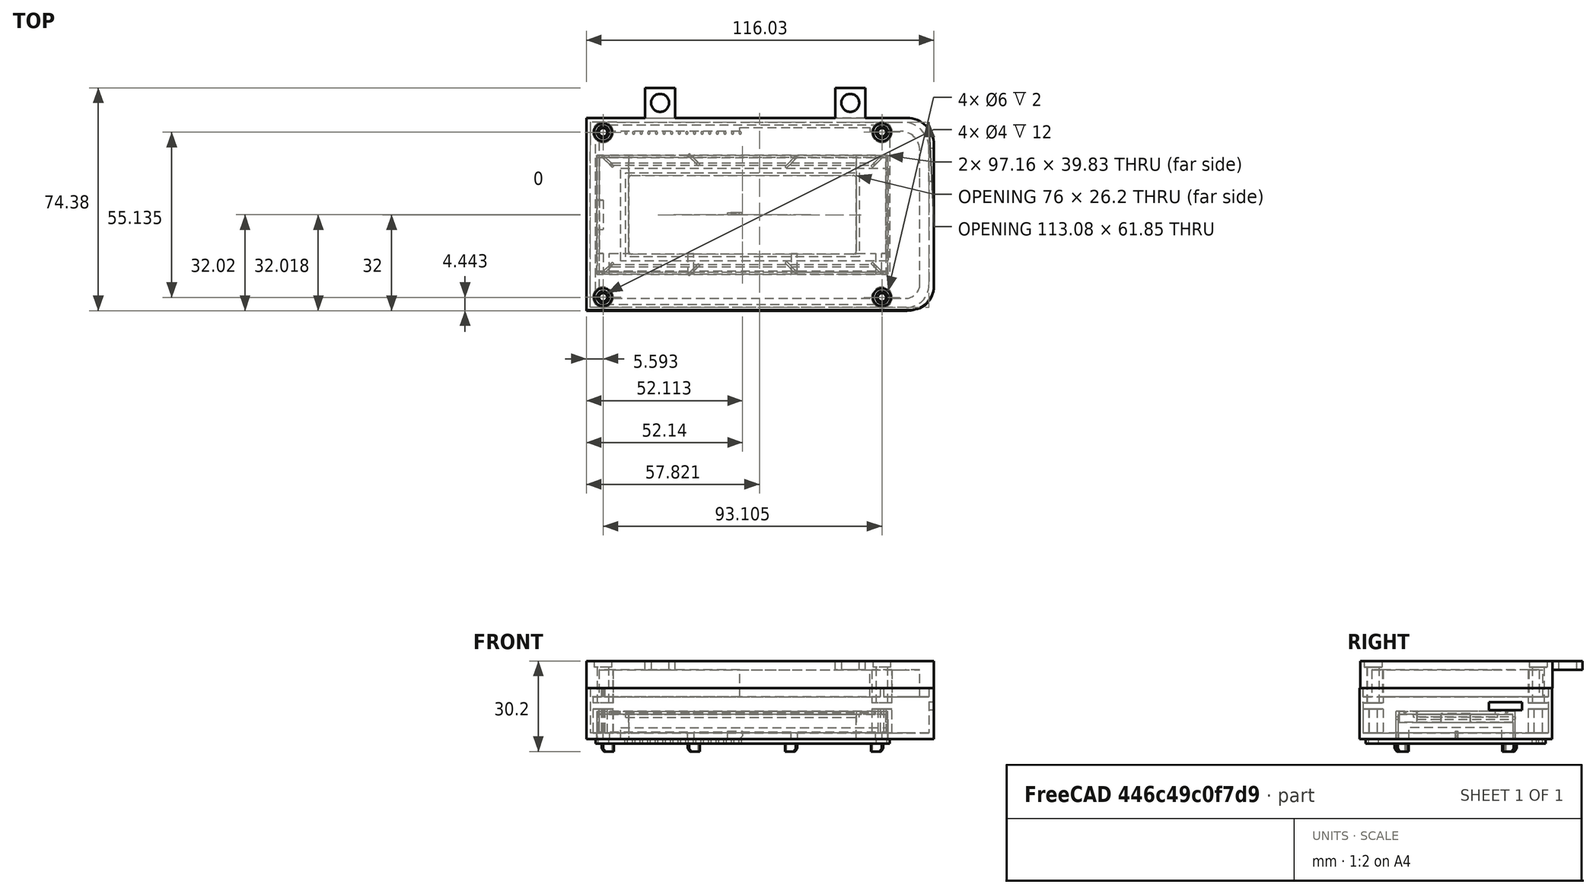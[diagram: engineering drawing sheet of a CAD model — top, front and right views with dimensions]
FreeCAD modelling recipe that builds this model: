
FCSTD DOCUMENT  (FreeCAD 0.18R13666 (Git))
Label: meteostation-lcd
License: CC-BY 3.0
LicenseURL: http://creativecommons.org/licenses/by/3.0/
objects: Sketcher::SketchObject×26, PartDesign::Body×14, PartDesign::Pocket×11, Part::Feature×10, App::DocumentObjectGroup×8, PartDesign::Pad×7, Part::Extrusion×5, Part::MultiFuse×4, PartDesign::FeatureBase×3, PartDesign::LinearPattern×1, Part::Mirroring×1, Part::Compound×1, PartDesign::Plane×1, PartDesign::ShapeBinder×1, App::Part×1, Mesh::Feature×1, PartDesign::Fillet×1, PartDesign::Hole×1
note: 106 computed .brp shape members not serialized (recipe doc carries the construction recipe); baked Part::Feature solids carry a one-line shape summary decoded from their .brp

FEATURE [Sketcher::SketchObject] Sketch001  label="backlight-sketch"
  MapMode = 5
  Support = -> [XY_Plane003]
  sketch-geometry (4):
    g0: LineSegment StartX=-40.6 StartY=15.5 StartZ=0 EndX=48.6 EndY=15.5 EndZ=0
    g1: LineSegment StartX=48.6 StartY=15.5 StartZ=0 EndX=48.6 EndY=-15.5 EndZ=0
    g2: LineSegment StartX=48.6 StartY=-15.5 StartZ=0 EndX=-40.6 EndY=-15.5 EndZ=0
    g3: LineSegment StartX=-40.6 StartY=-15.5 StartZ=0 EndX=-40.6 EndY=15.5 EndZ=0
  constraints (12):
    c: Coincident(g0,g1)
    c: Coincident(g1,g2)
    c: Coincident(g2,g3)
    c: Coincident(g3,g0)
    c: Horizontal(g0)
    c: Horizontal(g2)
    c: Vertical(g1)
    c: Vertical(g3)
    c: DistanceX(g-1,g1) = 48.6
    c: Symmetric(g0,g2,g-1)
    c: DistanceY(g-1,g0) = 15.5
    c: DistanceX(g-1,g0) = -40.6
FEATURE [PartDesign::Pad] Pad001  label="backlight"
  Length = 3.7
  Length2 = 100
  Profile = -> Sketch001
  Type = 0
FEATURE [Sketcher::SketchObject] Sketch002  label="metal-cover-main-sketch"
  MapMode = 5
  Support = -> [XY_Plane004]
  sketch-geometry (4):
    g0: LineSegment StartX=-48.5 StartY=19.85 StartZ=0 EndX=48.5 EndY=19.85 EndZ=0
    g1: LineSegment StartX=48.5 StartY=19.85 StartZ=0 EndX=48.5 EndY=-19.85 EndZ=0
    g2: LineSegment StartX=48.5 StartY=-19.85 StartZ=0 EndX=-48.5 EndY=-19.85 EndZ=0
    g3: LineSegment StartX=-48.5 StartY=-19.85 StartZ=0 EndX=-48.5 EndY=19.85 EndZ=0
  constraints (11):
    c: Coincident(g0,g1)
    c: Coincident(g1,g2)
    c: Coincident(g2,g3)
    c: Coincident(g3,g0)
    c: Horizontal(g0)
    c: Horizontal(g2)
    c: Vertical(g1)
    c: Vertical(g3)
    c: Symmetric(g0,g1,g-1)
    c: DistanceX(g0) = 97
    c: DistanceY(g1) = -39.7
FEATURE [PartDesign::Pad] Pad002  label="metal-cover"
  Length = 9.2
  Length2 = 100
  Profile = -> Sketch002
  Type = 0
FEATURE [Sketcher::SketchObject] Sketch003  label="bottom-cutout-1-sketch"
  ExternalGeometry = -> [Pad002]
  MapMode = 5
  Placement = pos=(0,0,0) rot=(1,0,0;3.14159rad)
  Support = -> [Pad002]
  sketch-geometry (5):
    g0: LineSegment StartX=-47.8 StartY=19.15 StartZ=0 EndX=47.8 EndY=19.15 EndZ=0
    g1: LineSegment StartX=47.8 StartY=19.15 StartZ=0 EndX=47.8 EndY=-19.15 EndZ=0
    g2: LineSegment StartX=47.8 StartY=-19.15 StartZ=0 EndX=-47.8 EndY=-19.15 EndZ=0
    g3: LineSegment StartX=-47.8 StartY=-19.15 StartZ=0 EndX=-47.8 EndY=19.15 EndZ=0
    g4: LineSegment [constr] StartX=-48.5 StartY=19.85 StartZ=0 EndX=-47.8 EndY=19.15 EndZ=0
  constraints (13):
    c: Coincident(g0,g1)
    c: Coincident(g1,g2)
    c: Coincident(g2,g3)
    c: Coincident(g3,g0)
    c: Horizontal(g0)
    c: Horizontal(g2)
    c: Vertical(g1)
    c: Vertical(g3)
    c: Symmetric(g0,g1,g-1)
    c: Coincident(g4,g-3)
    c: Coincident(g4,g0)
    c: Angle(g4,g-3) = 0.785398
    c: DistanceX(g0,g4) = -0.7
FEATURE [PartDesign::Pocket] Pocket  label="bottom-cutout-1"
  BaseFeature = -> Pad002
  Length = 8.2
  Length2 = 100
  Profile = -> Sketch003
  Type = 0
FEATURE [Sketcher::SketchObject] Sketch004  label="side-cutout-2-sketch"
  ExternalGeometry = -> [Pocket]
  MapMode = 5
  Placement = pos=(48.5,0,0) rot=(0.57735,0.57735,0.57735;2.0944rad)
  Support = -> [Pocket]
  sketch-geometry (7):
    g0: LineSegment StartX=19.15 StartY=5.5 StartZ=0 EndX=-19.15 EndY=5.5 EndZ=0
    g1: LineSegment StartX=-19.15 StartY=5.5 StartZ=0 EndX=-19.15 EndY=0 EndZ=0
    g2: LineSegment [constr] StartX=-19.15 StartY=0 StartZ=0 EndX=19.15 EndY=0 EndZ=0
    g3: LineSegment StartX=19.15 StartY=0 StartZ=0 EndX=19.15 EndY=5.5 EndZ=0
    g4: LineSegment StartX=-19.15 StartY=0 StartZ=0 EndX=-19.15 EndY=-1 EndZ=0
    g5: LineSegment StartX=-19.15 StartY=-1 StartZ=0 EndX=19.15 EndY=-1 EndZ=0
    g6: LineSegment StartX=19.15 StartY=-1 StartZ=0 EndX=19.15 EndY=0 EndZ=0
  constraints (19):
    c: Coincident(g0,g1)
    c: Coincident(g1,g2)
    c: Coincident(g2,g3)
    c: Coincident(g3,g0)
    c: Horizontal(g0)
    c: Horizontal(g2)
    c: Vertical(g1)
    c: Vertical(g3)
    c: Symmetric(g0,g0,g-2)
    c: DistanceY(g-3,g0) = -3.7
    c: Coincident(g2,g-4)
    c: Coincident(g4,g5)
    c: Coincident(g5,g6)
    c: Horizontal(g5)
    c: Vertical(g4)
    c: Vertical(g6)
    c: Coincident(g6,g2)
    c: Coincident(g4,g1)
    c: DistanceY(g4) = -1
FEATURE [PartDesign::Pocket] Pocket001  label="side-cutout-2"
  BaseFeature = -> Pocket
  Length = 5
  Length2 = 100
  Profile = -> Sketch004
  Type = 1
FEATURE [Sketcher::SketchObject] Sketch005  label="front-cutout-3-sketch"
  ExternalGeometry = -> [Pocket001]
  MapMode = 5
  Placement = pos=(0,0,5.5) rot=(1,0,0;3.14159rad)
  Support = -> [Pocket001]
  sketch-geometry (21):
    g0: LineSegment [constr] StartX=-48.5 StartY=12.85 StartZ=0 EndX=48.5 EndY=12.85 EndZ=0
    g1: LineSegment StartX=-16.25 StartY=12.85 StartZ=0 EndX=16.25 EndY=12.85 EndZ=0
    g2: LineSegment StartX=16.25 StartY=12.85 StartZ=0 EndX=16.25 EndY=18.85 EndZ=0
    g3: LineSegment StartX=16.25 StartY=18.85 StartZ=0 EndX=-16.25 EndY=18.85 EndZ=0
    g4: LineSegment StartX=-16.25 StartY=18.85 StartZ=0 EndX=-16.25 EndY=12.85 EndZ=0
    g5: LineSegment StartX=-44.45 StartY=12.85 StartZ=0 EndX=-18.25 EndY=12.85 EndZ=0
    g6: LineSegment StartX=-18.25 StartY=12.85 StartZ=0 EndX=-18.25 EndY=18.85 EndZ=0
    g7: LineSegment StartX=-18.25 StartY=18.85 StartZ=0 EndX=-44.45 EndY=18.85 EndZ=0
    g8: LineSegment StartX=-44.45 StartY=18.85 StartZ=0 EndX=-44.45 EndY=12.85 EndZ=0
    g9: LineSegment StartX=-51.45 StartY=12.85 StartZ=0 EndX=-46.45 EndY=12.85 EndZ=0
    g10: LineSegment StartX=-46.45 StartY=12.85 StartZ=0 EndX=-46.45 EndY=18.85 EndZ=0
    g11: LineSegment StartX=-46.45 StartY=18.85 StartZ=0 EndX=-51.45 EndY=18.85 EndZ=0
    g12: LineSegment StartX=-51.45 StartY=18.85 StartZ=0 EndX=-51.45 EndY=12.85 EndZ=0
    g13: LineSegment StartX=18.25 StartY=12.85 StartZ=0 EndX=44.45 EndY=12.85 EndZ=0
    g14: LineSegment StartX=44.45 StartY=12.85 StartZ=0 EndX=44.45 EndY=18.85 EndZ=0
    g15: LineSegment StartX=44.45 StartY=18.85 StartZ=0 EndX=18.25 EndY=18.85 EndZ=0
    g16: LineSegment StartX=18.25 StartY=18.85 StartZ=0 EndX=18.25 EndY=12.85 EndZ=0
    g17: LineSegment StartX=46.45 StartY=12.85 StartZ=0 EndX=51.45 EndY=12.85 EndZ=0
    g18: LineSegment StartX=51.45 StartY=12.85 StartZ=0 EndX=51.45 EndY=18.85 EndZ=0
    g19: LineSegment StartX=51.45 StartY=18.85 StartZ=0 EndX=46.45 EndY=18.85 EndZ=0
    g20: LineSegment StartX=46.45 StartY=18.85 StartZ=0 EndX=46.45 EndY=12.85 EndZ=0
  constraints (62):
    c: Horizontal(g0)
    c: PointOnObject(g0,g-4)
    c: Symmetric(g0,g0,g-2)
    c: DistanceY(g0,g-4) = 7
    c: Coincident(g1,g2)
    c: Coincident(g2,g3)
    c: Coincident(g3,g4)
    c: Coincident(g4,g1)
    c: Horizontal(g1)
    c: Horizontal(g3)
    c: Vertical(g2)
    c: Vertical(g4)
    c: PointOnObject(g1,g0)
    c: Symmetric(g1,g1,g-2)
    c: DistanceX(g1,g1) = 32.5
    c: Coincident(g5,g6)
    c: Coincident(g6,g7)
    c: Coincident(g7,g8)
    c: Coincident(g8,g5)
    c: Horizontal(g5)
    c: Horizontal(g7)
    c: Vertical(g6)
    c: Vertical(g8)
    c: PointOnObject(g5,g0)
    c: DistanceX(g5,g5) = 26.2
    c: DistanceX(g5,g1) = 2
    c: PointOnObject(g6,g3)
    c: Coincident(g9,g10)
    c: Coincident(g10,g11)
    c: Coincident(g11,g12)
    c: Coincident(g12,g9)
    c: Horizontal(g9)
    c: Horizontal(g11)
    c: Vertical(g10)
    c: Vertical(g12)
    c: PointOnObject(g9,g0)
    c: DistanceX(g5,g9) = -2
    c: PointOnObject(g10,g7)
    c: DistanceY(g11,g-4) = 1
    c: DistanceX(g11,g10) = 5
    c: Coincident(g13,g14)
    c: Coincident(g14,g15)
    c: Coincident(g15,g16)
    c: Coincident(g16,g13)
    c: Horizontal(g13)
    c: Horizontal(g15)
    c: Vertical(g14)
    c: Vertical(g16)
    c: Symmetric(g13,g5,g-2)
    c: PointOnObject(g15,g3)
    c: Symmetric(g13,g5,g-2)
    c: Coincident(g17,g18)
    c: Coincident(g18,g19)
    c: Coincident(g19,g20)
    c: Coincident(g20,g17)
    c: Horizontal(g17)
    c: Horizontal(g19)
    c: Vertical(g18)
    c: Vertical(g20)
    c: Symmetric(g17,g9,g-2)
    c: PointOnObject(g19,g15)
    c: Symmetric(g17,g9,g-2)
FEATURE [PartDesign::Pocket] Pocket002  label="front-cutout-3"
  BaseFeature = -> Pocket001
  Length = 5
  Length2 = 100
  Profile = -> Sketch005
  Type = 1
FEATURE [Sketcher::SketchObject] Sketch006  label="top-cutout-4-sketch"
  MapMode = 5
  Placement = pos=(0,-12.85,0) rot=(1,0,0;1.5708rad)
  Support = -> [Pocket002]
  sketch-geometry (8):
    g0: LineSegment StartX=-37 StartY=13.1 StartZ=0 EndX=37 EndY=13.1 EndZ=0
    g1: LineSegment StartX=38 StartY=12.1 StartZ=0 EndX=38 EndY=-12.1 EndZ=0
    g2: LineSegment StartX=37 StartY=-13.1 StartZ=0 EndX=-37 EndY=-13.1 EndZ=0
    g3: LineSegment StartX=-38 StartY=-12.1 StartZ=0 EndX=-38 EndY=12.1 EndZ=0
    g4: ArcOfCircle CenterX=-37 CenterY=12.1 CenterZ=0 NormalX=0 NormalY=0 NormalZ=1 AngleXU=0 Radius=1 StartAngle=1.5708 EndAngle=3.14159
    g5: ArcOfCircle CenterX=37 CenterY=12.1 CenterZ=0 NormalX=0 NormalY=0 NormalZ=1 AngleXU=0 Radius=1 StartAngle=0 EndAngle=1.5708
    g6: ArcOfCircle CenterX=37 CenterY=-12.1 CenterZ=0 NormalX=0 NormalY=0 NormalZ=1 AngleXU=0 Radius=1 StartAngle=4.71239 EndAngle=6.28319
    g7: ArcOfCircle CenterX=-37 CenterY=-12.1 CenterZ=0 NormalX=0 NormalY=0 NormalZ=1 AngleXU=0 Radius=1 StartAngle=3.14159 EndAngle=4.71239
  constraints (19):
    c: Horizontal(g0)
    c: Horizontal(g2)
    c: Vertical(g1)
    c: Vertical(g3)
    c: Tangent(g0,g4)
    c: Tangent(g3,g4)
    c: Tangent(g0,g5)
    c: Tangent(g1,g5)
    c: Tangent(g1,g6)
    c: Tangent(g2,g6)
    c: Tangent(g2,g7)
    c: Tangent(g3,g7)
    c: Radius(g4) = 1
    c: Equal(g4,g7)
    c: Equal(g7,g5)
    c: Equal(g5,g6)
    c: Symmetric(g4,g6,g-1)
    c: DistanceY(g0,g2) = -26.2
    c: DistanceX(g3,g1) = 76
FEATURE [PartDesign::Pocket] Pocket003  label="top-cutout-4"
  BaseFeature = -> Pocket002
  Length = 5
  Length2 = 100
  Profile = -> Sketch006
  Type = 1
FEATURE [Sketcher::SketchObject] Sketch007  label="top-slots-sketch"
  ExternalGeometry = -> [Pocket003]
  MapMode = 5
  Placement = pos=(48.5,0,0) rot=(0.57735,0.57735,0.57735;2.0944rad)
  Support = -> [Pocket003]
  sketch-geometry (8):
    g0: ArcOfCircle CenterX=-43.7 CenterY=7 CenterZ=0 NormalX=0 NormalY=0 NormalZ=1 AngleXU=0 Radius=0.4 StartAngle=1.57078 EndAngle=4.7124
    g1: ArcOfCircle CenterX=43.7 CenterY=7 CenterZ=0 NormalX=0 NormalY=0 NormalZ=1 AngleXU=0 Radius=0.4 StartAngle=4.71239 EndAngle=7.85398
    g2: LineSegment StartX=-43.7 StartY=6.6 StartZ=0 EndX=43.7 EndY=6.6 EndZ=0
    g3: LineSegment StartX=-43.7 StartY=7.4 StartZ=0 EndX=43.7 EndY=7.4 EndZ=0
    g4: ArcOfCircle CenterX=-43.7 CenterY=-7 CenterZ=0 NormalX=0 NormalY=0 NormalZ=1 AngleXU=0 Radius=0.4 StartAngle=1.5708 EndAngle=4.71239
    g5: ArcOfCircle CenterX=43.7 CenterY=-7 CenterZ=0 NormalX=0 NormalY=0 NormalZ=1 AngleXU=0 Radius=0.4 StartAngle=4.71239 EndAngle=7.85398
    g6: LineSegment StartX=-43.7 StartY=-7.4 StartZ=0 EndX=43.7 EndY=-7.4 EndZ=0
    g7: LineSegment StartX=-43.7 StartY=-6.6 StartZ=0 EndX=43.7 EndY=-6.6 EndZ=0
  constraints (26):
    c: Tangent(g0,g2)
    c: Tangent(g0,g3)
    c: Tangent(g1,g2)
    c: Tangent(g1,g3)
    c: Coincident(g0,g3)
    c: Coincident(g0,g2)
    c: Coincident(g2,g1)
    c: Coincident(g3,g1)
    c: Horizontal(g2)
    c: Radius(g1) = 0.4
    c: Symmetric(g0,g1,g-2)
    c: DistanceY(g0,g-3) = 1.8
    c: DistanceX(g0,g1) = 87.4
    c: Tangent(g4,g6)
    c: Tangent(g4,g7)
    c: Tangent(g5,g6)
    c: Tangent(g5,g7)
    c: Coincident(g4,g7)
    c: Coincident(g4,g6)
    c: Coincident(g6,g5)
    c: Coincident(g7,g5)
    c: Horizontal(g6)
    c: Equal(g4,g5)
    c: Equal(g5,g1)
    c: Symmetric(g4,g0,g-1)
    c: Symmetric(g5,g1,g-1)
FEATURE [PartDesign::Pocket] Pocket004  label="top-slots"
  BaseFeature = -> Pocket003
  Length = 0.5
  Length2 = 100
  Profile = -> Sketch007
  Type = 0
FEATURE [Sketcher::SketchObject] Sketch008
  ExternalGeometry = -> [Pocket004]
  MapMode = 5
  Placement = pos=(0,19.85,0) rot=(0,0.707107,0.707107;3.14159rad)
  Support = -> [Pocket004]
  sketch-geometry (4):
    g0: LineSegment StartX=-4.9 StartY=7.5 StartZ=0 EndX=4.9 EndY=7.5 EndZ=0
    g1: LineSegment StartX=4.9 StartY=7.5 StartZ=0 EndX=4.9 EndY=2.5 EndZ=0
    g2: LineSegment StartX=4.9 StartY=2.5 StartZ=0 EndX=-4.9 EndY=2.5 EndZ=0
    g3: LineSegment StartX=-4.9 StartY=2.5 StartZ=0 EndX=-4.9 EndY=7.5 EndZ=0
  constraints (12):
    c: Coincident(g0,g1)
    c: Coincident(g1,g2)
    c: Coincident(g2,g3)
    c: Coincident(g3,g0)
    c: Horizontal(g0)
    c: Horizontal(g2)
    c: Vertical(g1)
    c: Vertical(g3)
    c: Symmetric(g0,g0,g-2)
    c: DistanceY(g0,g-3) = 0.7
    c: DistanceX(g0) = 9.8
    c: DistanceY(g1) = -5
FEATURE [PartDesign::Pocket] Pocket005  label="side-cutout-5"
  BaseFeature = -> Pocket004
  Length = 2
  Length2 = 100
  Profile = -> Sketch008
  Type = 0
FEATURE [App::DocumentObjectGroup] Group  label="metal-cover-src"
FEATURE [Part::Feature] Pocket005001  label="metal-cover-final"
  shape: bbox 97 x 39.7 x 9.2 mm, 70 faces (baked)
FEATURE [App::DocumentObjectGroup] Group001  label="screen-src"
FEATURE [Part::Feature] Pad003001  label="screen-final"
  Placement = pos=(0,0,7.2) rot=(0,0,1;0rad)
  shape: bbox 78 x 28 x 1 mm, 6 faces (baked)
FEATURE [Sketcher::SketchObject] Sketch010  label="PCB-base-sketch"
  MapMode = 5
  Support = -> [XY_Plane001]
  sketch-geometry (4):
    g0: LineSegment StartX=-49.1 StartY=30.05 StartZ=0 EndX=49.1 EndY=30.05 EndZ=0
    g1: LineSegment StartX=49.1 StartY=30.05 StartZ=0 EndX=49.1 EndY=-30.05 EndZ=0
    g2: LineSegment StartX=49.1 StartY=-30.05 StartZ=0 EndX=-49.1 EndY=-30.05 EndZ=0
    g3: LineSegment StartX=-49.1 StartY=-30.05 StartZ=0 EndX=-49.1 EndY=30.05 EndZ=0
  constraints (11):
    c: Coincident(g0,g1)
    c: Coincident(g1,g2)
    c: Coincident(g2,g3)
    c: Coincident(g3,g0)
    c: Horizontal(g0)
    c: Horizontal(g2)
    c: Vertical(g1)
    c: Vertical(g3)
    c: Symmetric(g0,g1,g-1)
    c: DistanceX(g0) = 98.2
    c: DistanceY(g1) = -60.1
FEATURE [PartDesign::Pad] Pad003002  label="pcb-base"
  Length = 1.6
  Length2 = 100
  Profile = -> Sketch010
  Reversed = true
  Type = 0
FEATURE [Sketcher::SketchObject] Sketch011  label="drills-sketch"
  ExternalGeometry = -> [Pad003002]
  MapMode = 5
  Support = -> [Pad003002]
  sketch-geometry (4):
    g0: Circle CenterX=-46.4 CenterY=27.35 CenterZ=0 NormalX=0 NormalY=0 NormalZ=1 AngleXU=0 Radius=1.7
    g1: Circle CenterX=46.4 CenterY=27.35 CenterZ=0 NormalX=0 NormalY=0 NormalZ=1 AngleXU=0 Radius=1.7
    g2: Circle CenterX=-46.4 CenterY=-27.35 CenterZ=0 NormalX=0 NormalY=0 NormalZ=1 AngleXU=0 Radius=1.7
    g3: Circle CenterX=46.4 CenterY=-27.35 CenterZ=0 NormalX=0 NormalY=0 NormalZ=1 AngleXU=0 Radius=1.7
  constraints (9):
    c: Radius(g0) = 1.7
    c: DistanceX(g0,g-3) = -2.7
    c: DistanceY(g0,g-3) = 2.7
    c: Symmetric(g0,g1,g-2)
    c: Equal(g1,g3)
    c: Equal(g3,g2)
    c: Equal(g2,g0)
    c: Symmetric(g0,g2,g-1)
    c: Symmetric(g2,g3,g-2)
FEATURE [PartDesign::Pocket] Pocket005002  label="drills"
  BaseFeature = -> Pad003002
  Length = 5
  Length2 = 100
  Profile = -> Sketch011
  Type = 1
FEATURE [Sketcher::SketchObject] Sketch012  label="connector-drill-master-sketch"
  ExternalGeometry = -> [Pocket005002]
  MapMode = 5
  Support = -> [Pocket005002]
  sketch-geometry (1):
    g0: Circle CenterX=-38.9 CenterY=27.35 CenterZ=0 NormalX=0 NormalY=0 NormalZ=1 AngleXU=0 Radius=0.4
  constraints (3):
    c: Radius(g0) = 0.4
    c: DistanceX(g-3,g0) = 10.2
    c: DistanceY(g0,g-3) = 2.7
FEATURE [PartDesign::Pocket] Pocket005003  label="connector-drill-master"
  BaseFeature = -> Pocket005002
  Length = 5
  Length2 = 100
  Profile = -> Sketch012
  Type = 1
FEATURE [PartDesign::LinearPattern] LinearPattern
  BaseFeature = -> Pocket005003
  Direction = -> Sketch012 [H_Axis]
  Length = 38.1
  Occurrences = 16
  Originals = -> [Pocket005003]
FEATURE [App::DocumentObjectGroup] Group002  label="pcb-src"
FEATURE [Part::Feature] LinearPattern001  label="pcb-final"
  shape: bbox 98.2 x 60.1 x 1.6 mm, 26 faces (baked)
FEATURE [Sketcher::SketchObject] Sketch013  label="foot-master-sketch"
  MapMode = 5
  Placement = pos=(0,0,0) rot=(0,0.707107,0.707107;3.14159rad)
  Support = -> [XZ_Plane006]
  sketch-geometry (5):
    g0: LineSegment StartX=0 StartY=2.6 StartZ=0 EndX=0 EndY=1 EndZ=0
    g1: LineSegment StartX=0 StartY=1 StartZ=0 EndX=1 EndY=0 EndZ=0
    g2: LineSegment StartX=1 StartY=0 StartZ=0 EndX=5 EndY=0 EndZ=0
    g3: LineSegment StartX=5 StartY=0 StartZ=0 EndX=5 EndY=2.6 EndZ=0
    g4: LineSegment StartX=5 StartY=2.6 StartZ=0 EndX=0 EndY=2.6 EndZ=0
  constraints (15):
    c: Vertical(g0)
    c: Coincident(g0,g1)
    c: Coincident(g1,g2)
    c: Horizontal(g2)
    c: Coincident(g2,g3)
    c: Vertical(g3)
    c: Coincident(g3,g4)
    c: Coincident(g4,g0)
    c: Horizontal(g4)
    c: DistanceX(g4) = -5
    c: Angle(g2,g1) = 2.35619
    c: PointOnObject(g0,g-2)
    c: PointOnObject(g1,g-1)
    c: DistanceY(g3) = 2.6
    c: DistanceX(g-1,g1) = 1
FEATURE [PartDesign::Pad] Pad003003  label="foot-master"
  Length = 0.7
  Length2 = 100
  Placement = pos=(0,0,0) rot=(1,0,0;1.5708rad)
  Profile = -> Sketch013
  Type = 0
FEATURE [Part::Feature] Pad003003001  label="foot-1"
  Placement = pos=(-46.945,-19.355,-4.2) rot=(0.862856,0.357407,0.357407;1.71777rad)
  shape: bbox 4.031 x 4.031 x 2.6 mm, 7 faces (baked)
FEATURE [Part::Feature] Pad003003002  label="foot-002"
  Placement = pos=(-18.25,-19.85,-4.2) rot=(0.862856,0.357407,0.357407;1.71777rad)
  shape: bbox 4.031 x 4.031 x 2.6 mm, 7 faces (baked)
FEATURE [Part::Feature] Pad003003003  label="foot-003"
  Placement = pos=(46.45,-19.85,-4.2) rot=(0.281085,0.678598,0.678598;2.59356rad)
  shape: bbox 4.031 x 4.031 x 2.6 mm, 7 faces (baked)
FEATURE [Part::Feature] Pad003003004  label="foot-004"
  Placement = pos=(17.755,-19.645,-4.2) rot=(0.281085,0.678598,0.678598;2.59356rad)
  shape: bbox 4.031 x 4.031 x 2.6 mm, 7 faces (baked)
FEATURE [Part::MultiFuse] Fusion  label="front-feeth"
  Shapes = -> [Pad003003001,Pad003003002,Pad003003003,Pad003003004]
FEATURE [Part::Mirroring] Part__Mirroring  label="rear-feet"
  Base = (0,0,0)
  Normal = (0,1,0)
  Source = -> Fusion
FEATURE [Part::MultiFuse] Fusion001  label="feet"
  Shapes = -> [Part__Mirroring,Fusion]
FEATURE [App::DocumentObjectGroup] Group003  label="feet-src"
  Group = -> [Fusion001]
FEATURE [Part::Feature] Fusion002  label="feet-final"
  shape: bbox 93.89 x 40.69 x 2.6 mm, 56 faces, 8 solids (baked)
FEATURE [App::DocumentObjectGroup] Group004  label="inner-parts-src"
FEATURE [App::DocumentObjectGroup] Group005  label="src"
  Group = -> [Group,Group001,Group002,Group003,Group004]
FEATURE [Part::Feature] Pad003003005  label="frame-support001"
  shape: bbox 94.2 x 38.8 x 8.5 mm, 12 faces, 2 solids (baked)
FEATURE [Part::Feature] Pad003003006  label="backlight001"
  shape: bbox 89.2 x 31 x 3.7 mm, 6 faces (baked)
FEATURE [Part::Compound] Compound  label="lcd-4x20-backlight"
  Links = -> [Pad003003006,Pad003003005,Fusion002,LinearPattern001,Pad003001,Pocket005001]
FEATURE [Sketcher::SketchObject] Sketch015
  MapMode = 5
  sketch-geometry (4):
    g0: LineSegment StartX=-48.5104 StartY=19.8595 StartZ=0 EndX=48.6599 EndY=19.8595 EndZ=0
    g1: LineSegment StartX=48.6599 StartY=19.8595 StartZ=0 EndX=48.6599 EndY=-19.8947 EndZ=0
    g2: LineSegment StartX=48.6599 StartY=-19.8947 StartZ=0 EndX=-48.5104 EndY=-19.8947 EndZ=0
    g3: LineSegment StartX=-48.5104 StartY=-19.8947 StartZ=0 EndX=-48.5104 EndY=19.8595 EndZ=0
  constraints (8):
    c: Coincident(g0,g1)
    c: Coincident(g1,g2)
    c: Coincident(g2,g3)
    c: Coincident(g3,g0)
    c: Horizontal(g0)
    c: Horizontal(g2)
    c: Vertical(g1)
    c: Vertical(g3)
FEATURE [PartDesign::FeatureBase] BaseFeature
  BaseFeature = -> Compound
FEATURE [PartDesign::Body] Pad001Body
  Group = -> [Sketch001,Pad001]
  Origin = -> Origin003
  Tip = -> Pad001
FEATURE [PartDesign::Body] Pocket005Body
  Group = -> [Sketch002,Pad002,Sketch003,Pocket,Sketch004,Pocket001,Sketch005,Pocket002,Sketch006,Pocket003,Sketch007,Pocket004,Sketch008,Pocket005]
  Origin = -> Origin004
  Tip = -> Pocket005
FEATURE [PartDesign::Plane] DatumPlane
  AttachmentOffset = pos=(0,0,7.2) rot=(0,0,1;0rad)
  MapMode = 5
  Placement = pos=(0,0,7.2) rot=(0,0,1;0rad)
  Support = -> [XY_Plane005]
FEATURE [Sketcher::SketchObject] Sketch009  label="screen-sketch"
  MapMode = 5
  Placement = pos=(0,0,7.2) rot=(0,0,1;0rad)
  Support = -> [DatumPlane]
  sketch-geometry (4):
    g0: LineSegment StartX=-39 StartY=14 StartZ=0 EndX=39 EndY=14 EndZ=0
    g1: LineSegment StartX=39 StartY=14 StartZ=0 EndX=39 EndY=-14 EndZ=0
    g2: LineSegment StartX=39 StartY=-14 StartZ=0 EndX=-39 EndY=-14 EndZ=0
    g3: LineSegment StartX=-39 StartY=-14 StartZ=0 EndX=-39 EndY=14 EndZ=0
  constraints (11):
    c: Coincident(g0,g1)
    c: Coincident(g1,g2)
    c: Coincident(g2,g3)
    c: Coincident(g3,g0)
    c: Horizontal(g0)
    c: Horizontal(g2)
    c: Vertical(g1)
    c: Vertical(g3)
    c: Symmetric(g0,g1,g-1)
    c: DistanceX(g0) = 78
    c: DistanceY(g1) = -28
FEATURE [PartDesign::Pad] Pad003  label="screen"
  Length = 1
  Length2 = 100
  Placement = pos=(0,0,7.2) rot=(0,0,1;0rad)
  Profile = -> Sketch009
  Type = 0
FEATURE [PartDesign::Body] Pad003Body
  Group = -> [DatumPlane,Sketch009,Pad003]
  Origin = -> Origin005
  Tip = -> Pad003
FEATURE [PartDesign::Body] Pad003003Body
  Group = -> [Sketch013,Pad003003]
  Origin = -> Origin006
  Tip = -> Pad003003
FEATURE [PartDesign::ShapeBinder] ShapeBinder
  Support = -> [Compound]
FEATURE [Sketcher::SketchObject] Sketch014
  ExternalGeometry = -> [ShapeBinder]
  MapMode = 5
  sketch-geometry (8):
    g0: LineSegment StartX=-48.6064 StartY=19.9145 StartZ=0 EndX=48.5518 EndY=19.9145 EndZ=0
    g1: LineSegment StartX=48.5518 StartY=19.9145 StartZ=0 EndX=48.5518 EndY=-19.9179 EndZ=0
    g2: LineSegment StartX=48.5518 StartY=-19.9179 StartZ=0 EndX=-48.6064 EndY=-19.9179 EndZ=0
    g3: LineSegment StartX=-48.6064 StartY=-19.9179 StartZ=0 EndX=-48.6064 EndY=19.9145 EndZ=0
    g4: LineSegment StartX=63.8853 StartY=32.1532 StartZ=0 EndX=-52.1447 EndY=32.1532 EndZ=0
    g5: LineSegment StartX=-52.1447 StartY=32.1532 StartZ=0 EndX=-52.1447 EndY=-32.0168 EndZ=0
    g6: LineSegment StartX=-52.1447 StartY=-32.0168 StartZ=0 EndX=63.8853 EndY=-32.0168 EndZ=0
    g7: LineSegment StartX=63.8853 StartY=-32.0168 StartZ=0 EndX=63.8853 EndY=32.1532 EndZ=0
  constraints (18):
    c: Coincident(g0,g1)
    c: Coincident(g1,g2)
    c: Coincident(g2,g3)
    c: Coincident(g3,g0)
    c: Horizontal(g0)
    c: Horizontal(g2)
    c: Vertical(g1)
    c: Vertical(g3)
    c: Coincident(g4,g5)
    c: Coincident(g5,g6)
    c: Coincident(g6,g7)
    c: Coincident(g7,g4)
    c: Horizontal(g4)
    c: Horizontal(g6)
    c: Vertical(g5)
    c: Vertical(g7)
    c: DistanceX(g4,g4) = 116.03
    c: DistanceY(g5,g5) = 64.17
FEATURE [PartDesign::Body] LinearPatternBody
  Group = -> [Sketch010,Pad003002,Sketch011,Pocket005002,Sketch012,Pocket005003,LinearPattern,ShapeBinder]
  Origin = -> Origin001
  Tip = -> LinearPattern
FEATURE [PartDesign::Body] Body
  Origin = -> Origin007
FEATURE [PartDesign::Body] Body001
  Origin = -> Origin008
FEATURE [PartDesign::Body] Body002
  Origin = -> Origin009
FEATURE [PartDesign::Body] Body003
  Origin = -> Origin010
FEATURE [PartDesign::Body] Body004
  Origin = -> Origin011
FEATURE [PartDesign::Body] Body005
  Origin = -> Origin012
FEATURE [Sketcher::SketchObject] Sketch016  label="LCD-fitter"
  MapMode = 2
  Support = -> [Sketch015]
  sketch-geometry (8):
    g0: Circle CenterX=46.5412 CenterY=-27.5775 CenterZ=0 NormalX=0 NormalY=0 NormalZ=1 AngleXU=0 Radius=3.40904
    g1: Circle CenterX=46.5412 CenterY=-27.5775 CenterZ=0 NormalX=0 NormalY=0 NormalZ=1 AngleXU=0 Radius=1.40359
    g2: Circle CenterX=46.5582 CenterY=27.5573 CenterZ=0 NormalX=0 NormalY=0 NormalZ=1 AngleXU=0 Radius=3.39833
    g3: Circle CenterX=46.5582 CenterY=27.5573 CenterZ=0 NormalX=0 NormalY=0 NormalZ=1 AngleXU=0 Radius=1.39754
    g4: Circle CenterX=-46.5468 CenterY=27.5496 CenterZ=0 NormalX=0 NormalY=0 NormalZ=1 AngleXU=0 Radius=3.403
    g5: Circle CenterX=-46.5468 CenterY=27.5496 CenterZ=0 NormalX=0 NormalY=0 NormalZ=1 AngleXU=0 Radius=1.4134
    g6: Circle CenterX=-46.5358 CenterY=-27.5356 CenterZ=0 NormalX=0 NormalY=0 NormalZ=1 AngleXU=0 Radius=3.41269
    g7: Circle CenterX=-46.5358 CenterY=-27.5356 CenterZ=0 NormalX=0 NormalY=0 NormalZ=1 AngleXU=0 Radius=1.38539
  constraints (4):
    c: Coincident(g1,g0)
    c: Coincident(g3,g2)
    c: Coincident(g5,g4)
    c: Coincident(g7,g6)
FEATURE [App::DocumentObjectGroup] Group006  label="Grup"
  Group = -> [Sketch015,Sketch014,Sketch016]
FEATURE [Part::Extrusion] Extrude  label="Extrude-lcd-fitter"
  Base = -> Sketch016
  Dir = (0,0,1)
  DirMode = 2
  FaceMakerClass = Part::FaceMakerBullseye
  LengthFwd = 10
  LengthRev = 0
  Solid = true
  Symmetric = false
FEATURE [Part::Extrusion] Extrude002
  Base = -> Sketch014
  Dir = (0,0,1)
  DirMode = 2
  FaceMakerClass = Part::FaceMakerBullseye
  LengthFwd = 17
  LengthRev = 0
  Solid = true
  Symmetric = false
FEATURE [Sketcher::SketchObject] Sketch  label="frame-support-sketch"
  MapMode = 5
  Placement = pos=(0,0,17) rot=(0,0,1;0rad)
  Support = -> [Extrude002]
  sketch-geometry (8):
    g0: LineSegment StartX=-47.1 StartY=19.4 StartZ=0 EndX=47.1 EndY=19.4 EndZ=0
    g1: LineSegment StartX=47.1 StartY=19.4 StartZ=0 EndX=47.1 EndY=15.9 EndZ=0
    g2: LineSegment StartX=47.1 StartY=15.9 StartZ=0 EndX=-47.1 EndY=15.9 EndZ=0
    g3: LineSegment StartX=-47.1 StartY=15.9 StartZ=0 EndX=-47.1 EndY=19.4 EndZ=0
    g4: LineSegment StartX=-47.1 StartY=-19.4 StartZ=0 EndX=47.1 EndY=-19.4 EndZ=0
    g5: LineSegment StartX=47.1 StartY=-19.4 StartZ=0 EndX=47.1 EndY=-15.9 EndZ=0
    g6: LineSegment StartX=47.1 StartY=-15.9 StartZ=0 EndX=-47.1 EndY=-15.9 EndZ=0
    g7: LineSegment StartX=-47.1 StartY=-15.9 StartZ=0 EndX=-47.1 EndY=-19.4 EndZ=0
  constraints (23):
    c: Coincident(g0,g1)
    c: Coincident(g1,g2)
    c: Coincident(g2,g3)
    c: Coincident(g3,g0)
    c: Horizontal(g0)
    c: Horizontal(g2)
    c: Vertical(g1)
    c: Vertical(g3)
    c: Symmetric(g0,g0,g-2)
    c: DistanceX(g0) = 94.2
    c: DistanceY(g1) = -3.5
    c: Coincident(g4,g5)
    c: Coincident(g5,g6)
    c: Coincident(g6,g7)
    c: Coincident(g7,g4)
    c: Horizontal(g4)
    c: Horizontal(g6)
    c: Vertical(g5)
    c: Vertical(g7)
    c: Symmetric(g6,g5,g-2)
    c: Symmetric(g2,g6,g-1)
    c: Symmetric(g4,g0,g-1)
    c: DistanceY(g0,g4) = -38.8
FEATURE [PartDesign::Pad] Pad  label="frame-support"
  BaseFeature = -> BaseFeature
  Length = 8.5
  Length2 = 100
  Profile = -> Sketch
  Type = 0
FEATURE [PartDesign::Body] PadBody
  BaseFeature = -> Compound
  Group = -> [BaseFeature,Sketch,Pad]
  Origin = -> Origin002
  Tip = -> Pad
FEATURE [App::Part] Part
  Group = -> [LinearPatternBody,PadBody,Pad001Body,Pocket005Body,Pad003Body,Pad003003Body,Body,Body001,Body002,Body003,Body004,Body005]
  License = CC BY 3.0
  LicenseURL = http://creativecommons.org/licenses/by/3.0/
  Origin = -> Origin
FEATURE [Sketcher::SketchObject] Sketch017
  MapMode = 5
  Placement = pos=(0,0,17) rot=(0,0,1;0rad)
  Support = -> [Extrude002]
  sketch-geometry (10):
    g0: LineSegment StartX=-41.9737 StartY=30.9037 StartZ=0 EndX=53.4751 EndY=30.9037 EndZ=0
    g1: LineSegment StartX=62.2216 StartY=22.1573 StartZ=0 EndX=62.2216 EndY=-23.4335 EndZ=0
    g2: LineSegment StartX=54.7113 StartY=-30.9438 StartZ=0 EndX=-43.3111 EndY=-30.9438 EndZ=0
    g3: LineSegment StartX=-50.8604 StartY=-23.3945 StartZ=0 EndX=-50.8604 EndY=22.017 EndZ=0
    g4: ArcOfCircle CenterX=53.4751 CenterY=22.1573 CenterZ=0 NormalX=0 NormalY=0 NormalZ=1 AngleXU=0 Radius=8.74646 StartAngle=0 EndAngle=1.5708
    g5: ArcOfCircle CenterX=54.7113 CenterY=-23.4335 CenterZ=0 NormalX=0 NormalY=0 NormalZ=1 AngleXU=0 Radius=7.51029 StartAngle=4.71239 EndAngle=6.28319
    g6: LineSegment StartX=-41.9737 StartY=30.9037 StartZ=0 EndX=-50.8604 EndY=30.9037 EndZ=0
    g7: LineSegment StartX=-50.8604 StartY=30.9037 StartZ=0 EndX=-50.8604 EndY=22.017 EndZ=0
    g8: LineSegment StartX=-43.3111 StartY=-30.9438 StartZ=0 EndX=-50.8604 EndY=-30.9438 EndZ=0
    g9: LineSegment StartX=-50.8604 StartY=-30.9438 StartZ=0 EndX=-50.8604 EndY=-23.3945 EndZ=0
  constraints (14):
    c: Horizontal(g0)
    c: Horizontal(g2)
    c: Vertical(g1)
    c: Vertical(g3)
    c: Tangent(g0,g4) = 1.5708
    c: Tangent(g1,g4) = 1.5708
    c: Tangent(g1,g5) = 1.5708
    c: Tangent(g2,g5) = 1.5708
    c: Coincident(g6,g7)
    c: Horizontal(g6)
    c: Vertical(g7)
    c: Coincident(g8,g9)
    c: Horizontal(g8)
    c: Vertical(g9)
FEATURE [PartDesign::FeatureBase] BaseFeature001
  BaseFeature = -> Extrude002
FEATURE [PartDesign::Pocket] Pocket005004
  BaseFeature = -> BaseFeature001
  Length = 15
  Length2 = 100
  Profile = -> Sketch017
  Type = 0
FEATURE [Sketcher::SketchObject] Sketch021  label="Backplate"
  sketch-geometry (18):
    g0: Circle CenterX=46.5412 CenterY=-27.5775 CenterZ=0 NormalX=0 NormalY=0 NormalZ=1 AngleXU=0 Radius=3
    g1: Circle CenterX=46.5582 CenterY=27.5573 CenterZ=0 NormalX=0 NormalY=0 NormalZ=1 AngleXU=0 Radius=3
    g2: Circle CenterX=-46.5468 CenterY=27.5496 CenterZ=0 NormalX=0 NormalY=0 NormalZ=1 AngleXU=0 Radius=3
    g3: Circle CenterX=-46.5358 CenterY=-27.5356 CenterZ=0 NormalX=0 NormalY=0 NormalZ=1 AngleXU=0 Radius=3
    g4: LineSegment StartX=54.8484 StartY=32.364 StartZ=0 EndX=40.9746 EndY=32.364 EndZ=0
    g5: LineSegment StartX=-52.1449 StartY=23.2907 StartZ=0 EndX=-52.1449 EndY=-23.9793 EndZ=0
    g6: LineSegment StartX=-44.3535 StartY=-31.7707 StartZ=0 EndX=56.0938 EndY=-31.7707 EndZ=0
    g7: LineSegment StartX=63.8884 StartY=-23.976 StartZ=0 EndX=63.8884 EndY=23.324 EndZ=0
    g8: ArcOfCircle CenterX=54.8484 CenterY=23.324 CenterZ=0 NormalX=0 NormalY=0 NormalZ=1 AngleXU=0 Radius=9.04 StartAngle=0 EndAngle=1.5708
    g9: ArcOfCircle CenterX=56.0938 CenterY=-23.976 CenterZ=0 NormalX=0 NormalY=0 NormalZ=1 AngleXU=0 Radius=7.79468 StartAngle=4.71239 EndAngle=6.28319
    g10: LineSegment StartX=-32.5121 StartY=32.364 StartZ=0 EndX=-43.0716 EndY=32.364 EndZ=0
    g11: LineSegment StartX=30.9746 StartY=32.364 StartZ=0 EndX=-22.5027 EndY=32.364 EndZ=0
    g12: LineSegment StartX=-43.0716 StartY=32.364 StartZ=0 EndX=-52.1449 EndY=32.364 EndZ=0
    g13: LineSegment StartX=-52.1449 StartY=32.364 StartZ=0 EndX=-52.1449 EndY=23.2907 EndZ=0
    g14: LineSegment StartX=-44.3535 StartY=-31.7707 StartZ=0 EndX=-52.1449 EndY=-31.7707 EndZ=0
    g15: LineSegment StartX=-52.1449 StartY=-31.7707 StartZ=0 EndX=-52.1449 EndY=-23.9793 EndZ=0
    g16: LineSegment StartX=30.9746 StartY=32.364 StartZ=0 EndX=40.9746 EndY=32.364 EndZ=0
    g17: LineSegment StartX=-32.5121 StartY=32.364 StartZ=0 EndX=-22.5027 EndY=32.364 EndZ=0
  constraints (31):
    c: Horizontal(g6)
    c: Vertical(g5)
    c: Vertical(g7)
    c: Tangent(g4,g8) = -1.5708
    c: Tangent(g7,g8) = -1.5708
    c: Tangent(g6,g9) = -1.5708
    c: Tangent(g7,g9) = -1.5708
    c: DistanceX(g10,g4) = 97.92
    c: DistanceY(g7,g7) = 47.3
    c: Radius(g8) = 9.04
    c: DistanceY(g5,g5) = 47.27
    c: Tangent(g4,g10)
    c: Tangent(g4,g11)
    c: Coincident(g12,g13)
    c: Horizontal(g12)
    c: Vertical(g13)
    c: Coincident(g13,g5)
    c: Coincident(g14,g15)
    c: Horizontal(g14)
    c: Vertical(g15)
    c: Coincident(g14,g6)
    c: Coincident(g15,g5)
    c: Radius(g2) = 3
    c: Radius(g1) = 3
    c: Radius(g3) = 3
    c: Radius(g0) = 3
    c: Coincident(g16,g11)
    c: Coincident(g16,g4)
    c: Horizontal(g16)
    c: Coincident(g17,g10)
    c: Coincident(g17,g11)
FEATURE [Part::Extrusion] Extrude004  label="Extrude-Backplate"
  Base = -> Sketch021
  Dir = (0,0,1)
  DirMode = 2
  FaceMakerClass = Part::FaceMakerBullseye
  LengthFwd = 9
  LengthRev = 0
  Solid = true
  Symmetric = false
FEATURE [Mesh::Feature] beveled_LCD_frame_20x4
FEATURE [Sketcher::SketchObject] Sketch022  label="Sketch-Hardware-lcd"
  MapMode = 5
  sketch-geometry (4):
    g0: LineSegment StartX=-48.5104 StartY=19.8595 StartZ=0 EndX=48.6599 EndY=19.8595 EndZ=0
    g1: LineSegment StartX=48.6599 StartY=19.8595 StartZ=0 EndX=48.6599 EndY=-19.8947 EndZ=0
    g2: LineSegment StartX=48.6599 StartY=-19.8947 StartZ=0 EndX=-48.5104 EndY=-19.8947 EndZ=0
    g3: LineSegment StartX=-48.5104 StartY=-19.8947 StartZ=0 EndX=-48.5104 EndY=19.8595 EndZ=0
  constraints (8):
    c: Coincident(g0,g1)
    c: Coincident(g1,g2)
    c: Coincident(g2,g3)
    c: Coincident(g3,g0)
    c: Horizontal(g0)
    c: Horizontal(g2)
    c: Vertical(g1)
    c: Vertical(g3)
FEATURE [Sketcher::SketchObject] Sketch023  label="fitter-back"
  MapMode = 2
  Support = -> [Sketch022]
  sketch-geometry (8):
    g0: Circle CenterX=46.5412 CenterY=-27.5775 CenterZ=0 NormalX=0 NormalY=0 NormalZ=1 AngleXU=0 Radius=3.40904
    g1: Circle CenterX=46.5412 CenterY=-27.5775 CenterZ=0 NormalX=0 NormalY=0 NormalZ=1 AngleXU=0 Radius=2
    g2: Circle CenterX=46.5582 CenterY=27.5573 CenterZ=0 NormalX=0 NormalY=0 NormalZ=1 AngleXU=0 Radius=3.39833
    g3: Circle CenterX=46.5582 CenterY=27.5573 CenterZ=0 NormalX=0 NormalY=0 NormalZ=1 AngleXU=0 Radius=2
    g4: Circle CenterX=-46.5468 CenterY=27.5496 CenterZ=0 NormalX=0 NormalY=0 NormalZ=1 AngleXU=0 Radius=3.403
    g5: Circle CenterX=-46.5468 CenterY=27.5496 CenterZ=0 NormalX=0 NormalY=0 NormalZ=1 AngleXU=0 Radius=2
    g6: Circle CenterX=-46.5358 CenterY=-27.5356 CenterZ=0 NormalX=0 NormalY=0 NormalZ=1 AngleXU=0 Radius=3.41269
    g7: Circle CenterX=-46.5358 CenterY=-27.5356 CenterZ=0 NormalX=0 NormalY=0 NormalZ=1 AngleXU=0 Radius=2
  constraints (8):
    c: Coincident(g1,g0)
    c: Coincident(g3,g2)
    c: Coincident(g5,g4)
    c: Coincident(g7,g6)
    c: Radius(g3) = 2
    c: Radius(g5) = 2
    c: Radius(g7) = 2
    c: Radius(g1) = 2
FEATURE [Part::Extrusion] Extrude005  label="Extrude-fitter-back"
  Base = -> Sketch023
  Dir = (0,0,1)
  DirMode = 2
  FaceMakerClass = Part::FaceMakerBullseye
  LengthFwd = 12
  LengthRev = 0
  Placement = pos=(0,0,-5) rot=(0,0,1;0rad)
  Solid = true
  Symmetric = false
FEATURE [PartDesign::FeatureBase] BaseFeature002
  BaseFeature = -> Extrude004
FEATURE [PartDesign::Fillet] Fillet
  Base = -> Pocket005004 [Edge1,Edge5]
  BaseFeature = -> Pocket005004
  Radius = 9
FEATURE [Sketcher::SketchObject] Sketch018  label="Sketch-Cable-IN"
  MapMode = 5
  Placement = pos=(63.8853,0,0) rot=(0.57735,0.57735,0.57735;2.0944rad)
  Support = -> [Fillet]
  sketch-geometry (4):
    g0: LineSegment StartX=22.1179 StartY=9.63754 StartZ=0 EndX=11.1179 EndY=9.63754 EndZ=0
    g1: LineSegment StartX=11.1179 StartY=9.63754 StartZ=0 EndX=11.1179 EndY=12.2375 EndZ=0
    g2: LineSegment StartX=11.1179 StartY=12.2375 StartZ=0 EndX=22.1179 EndY=12.2375 EndZ=0
    g3: LineSegment StartX=22.1179 StartY=12.2375 StartZ=0 EndX=22.1179 EndY=9.63754 EndZ=0
  constraints (10):
    c: Coincident(g0,g1)
    c: Coincident(g1,g2)
    c: Coincident(g2,g3)
    c: Coincident(g3,g0)
    c: Horizontal(g0)
    c: Horizontal(g2)
    c: Vertical(g1)
    c: Vertical(g3)
    c: DistanceX(g0,g0) = 11
    c: DistanceY(g1,g1) = 2.6
FEATURE [PartDesign::Pocket] Pocket005005
  BaseFeature = -> Fillet
  Length = 5
  Length2 = 100
  Profile = -> Sketch018
  Type = 0
FEATURE [PartDesign::Body] Body006
  BaseFeature = -> Extrude002
  Group = -> [BaseFeature001,Sketch017,Pocket005004,Fillet,Sketch018,Pocket005005]
  Origin = -> Origin013
  Tip = -> Pocket005005
FEATURE [Part::MultiFuse] Fusion003  label="Fusion-End"
  Shapes = -> [Pocket005005,Extrude]
FEATURE [Sketcher::SketchObject] Sketch030  label="Sketch-Suport"
  sketch-geometry (10):
    g0: LineSegment StartX=-22.5121 StartY=32.364 StartZ=0 EndX=-22.5121 EndY=42.364 EndZ=0
    g1: LineSegment StartX=-22.5121 StartY=42.364 StartZ=0 EndX=-32.5121 EndY=42.364 EndZ=0
    g2: LineSegment StartX=-32.5121 StartY=42.364 StartZ=0 EndX=-32.5121 EndY=32.364 EndZ=0
    g3: LineSegment StartX=40.9652 StartY=32.364 StartZ=0 EndX=40.9652 EndY=42.364 EndZ=0
    g4: LineSegment StartX=40.9652 StartY=42.364 StartZ=0 EndX=30.9652 EndY=42.364 EndZ=0
    g5: LineSegment StartX=30.9652 StartY=42.364 StartZ=0 EndX=30.9652 EndY=32.364 EndZ=0
    g6: Circle CenterX=-27.5121 CenterY=37.364 CenterZ=0 NormalX=0 NormalY=0 NormalZ=1 AngleXU=0 Radius=3
    g7: Circle CenterX=35.9652 CenterY=37.364 CenterZ=0 NormalX=0 NormalY=0 NormalZ=1 AngleXU=0 Radius=3
    g8: LineSegment StartX=40.9652 StartY=32.364 StartZ=0 EndX=30.9652 EndY=32.364 EndZ=0
    g9: LineSegment StartX=-32.5121 StartY=32.364 StartZ=0 EndX=-22.5121 EndY=32.364 EndZ=0
  constraints (26):
    c: Coincident(g0,g1)
    c: Coincident(g1,g2)
    c: Horizontal(g1)
    c: Vertical(g0)
    c: Vertical(g2)
    c: Coincident(g3,g4)
    c: Coincident(g4,g5)
    c: Horizontal(g4)
    c: Vertical(g3)
    c: Vertical(g5)
    c: DistanceX(g4,g4) = 10
    c: DistanceX(g1,g1) = 10
    c: DistanceY(g3,g3) = 10
    c: DistanceY(g0,g0) = 10
    c: Radius(g6) = 3
    c: Radius(g7) = 3
    c: DistanceY(g5,g7) = 5
    c: DistanceY(g0,g6) = 5
    c: DistanceX(g6,g0) = 5
    c: DistanceX(g7,g3) = 5
    c: Horizontal(g8)
    c: Coincident(g9,g2)
    c: Coincident(g9,g0)
    c: Horizontal(g9)
    c: PointOnObject(g8,g5)
    c: Coincident(g3,g8)
FEATURE [Part::Extrusion] Extrude007  label="Extrude-Suport"
  Base = -> Sketch030
  Dir = (0,0,1)
  DirMode = 2
  FaceMakerClass = Part::FaceMakerBullseye
  LengthFwd = 3
  LengthRev = 0
  Placement = pos=(0,0,6) rot=(0,0,1;0rad)
  Solid = true
  Symmetric = false
FEATURE [PartDesign::Body] Body007
  BaseFeature = -> Extrude004
  Group = -> [BaseFeature002,Sketch027,Pad003003007,Sketch028,Sketch029,Pocket005006,Hole]
  Origin = -> Origin014
  Tip = -> Hole
FEATURE [App::DocumentObjectGroup] Group007  label="BackPlate-group"
  Group = -> [Fusion004,Extrude004]
FEATURE [Sketcher::SketchObject] Sketch027  label="Voraback"
  MapMode = 2
  Support = -> [Body007]
  sketch-geometry (10):
    g0: LineSegment StartX=-41.9737 StartY=30.9037 StartZ=0 EndX=53.4751 EndY=30.9037 EndZ=0
    g1: LineSegment StartX=62.2216 StartY=22.1573 StartZ=0 EndX=62.2216 EndY=-23.4335 EndZ=0
    g2: LineSegment StartX=54.7113 StartY=-30.9438 StartZ=0 EndX=-43.3111 EndY=-30.9438 EndZ=0
    g3: LineSegment StartX=-50.8604 StartY=-23.3945 StartZ=0 EndX=-50.8604 EndY=22.017 EndZ=0
    g4: ArcOfCircle CenterX=53.4751 CenterY=22.1573 CenterZ=0 NormalX=0 NormalY=0 NormalZ=1 AngleXU=0 Radius=8.74646 StartAngle=0 EndAngle=1.5708
    g5: ArcOfCircle CenterX=54.7113 CenterY=-23.4335 CenterZ=0 NormalX=0 NormalY=0 NormalZ=1 AngleXU=0 Radius=7.51029 StartAngle=4.71239 EndAngle=6.28319
    g6: LineSegment StartX=-41.9737 StartY=30.9037 StartZ=0 EndX=-50.8604 EndY=30.9037 EndZ=0
    g7: LineSegment StartX=-50.8604 StartY=30.9037 StartZ=0 EndX=-50.8604 EndY=22.017 EndZ=0
    g8: LineSegment StartX=-43.3111 StartY=-30.9438 StartZ=0 EndX=-50.8604 EndY=-30.9438 EndZ=0
    g9: LineSegment StartX=-50.8604 StartY=-30.9438 StartZ=0 EndX=-50.8604 EndY=-23.3945 EndZ=0
  constraints (14):
    c: Horizontal(g0)
    c: Horizontal(g2)
    c: Vertical(g1)
    c: Vertical(g3)
    c: Tangent(g0,g4) = 1.5708
    c: Tangent(g1,g4) = 1.5708
    c: Tangent(g1,g5) = 1.5708
    c: Tangent(g2,g5) = 1.5708
    c: Coincident(g6,g7)
    c: Horizontal(g6)
    c: Vertical(g7)
    c: Coincident(g8,g9)
    c: Horizontal(g8)
    c: Vertical(g9)
FEATURE [PartDesign::Pad] Pad003003007
  BaseFeature = -> BaseFeature002
  Length = 3
  Length2 = 100
  Profile = -> Sketch027
  Reversed = true
  Type = 0
FEATURE [Sketcher::SketchObject] Sketch028  label="Screws-backplate"
  MapMode = 5
  Placement = pos=(0,0,9) rot=(0,0,1;0rad)
  Support = -> [Pocket005006]
  sketch-geometry (4):
    g0: Circle CenterX=46.5412 CenterY=-27.5775 CenterZ=0 NormalX=0 NormalY=0 NormalZ=1 AngleXU=0 Radius=2
    g1: Circle CenterX=46.5582 CenterY=27.5573 CenterZ=0 NormalX=0 NormalY=0 NormalZ=1 AngleXU=0 Radius=2
    g2: Circle CenterX=-46.5468 CenterY=27.5496 CenterZ=0 NormalX=0 NormalY=0 NormalZ=1 AngleXU=0 Radius=2
    g3: Circle CenterX=-46.5358 CenterY=-27.5356 CenterZ=0 NormalX=0 NormalY=0 NormalZ=1 AngleXU=0 Radius=2
  constraints (4):
    c: Radius(g1) = 2
    c: Radius(g2) = 2
    c: Radius(g3) = 2
    c: Radius(g0) = 2
FEATURE [Part::MultiFuse] Fusion004
  Placement = pos=(0,0,17) rot=(0,0,1;0rad)
  Shapes = -> [Extrude005,Body007,Extrude007]
FEATURE [Sketcher::SketchObject] Sketch029
  ExternalGeometry = -> [Pad003003007]
  MapMode = 5
  Placement = pos=(0,0,-3) rot=(1,0,0;3.14159rad)
  Support = -> [Pad003003007]
  sketch-geometry (12):
    g0: LineSegment StartX=-47.8604 StartY=27.9438 StartZ=0 EndX=54.3338 EndY=27.9438 EndZ=0
    g1: LineSegment StartX=59.2216 StartY=23.0561 StartZ=0 EndX=59.2216 EndY=-12.599 EndZ=0
    g2: LineSegment StartX=-47.8604 StartY=-27.9037 StartZ=0 EndX=-47.8604 EndY=27.9438 EndZ=0
    g3: ArcOfCircle CenterX=54.3338 CenterY=23.0561 CenterZ=0 NormalX=0 NormalY=0 NormalZ=1 AngleXU=0 Radius=4.88775 StartAngle=0 EndAngle=1.5708
    g4: LineSegment StartX=16.9753 StartY=-29.1037 StartZ=0 EndX=42.4722 EndY=-29.1037 EndZ=0
    g5: LineSegment StartX=42.4722 StartY=-29.1037 StartZ=0 EndX=42.4722 EndY=-27.9037 EndZ=0
    g6: LineSegment StartX=-0.881046 StartY=-29.1037 StartZ=0 EndX=16.9753 EndY=-29.1037 EndZ=0
    g7: LineSegment StartX=-0.881046 StartY=-27.9037 StartZ=0 EndX=-0.881046 EndY=-29.1037 EndZ=0
    g8: LineSegment StartX=-0.881046 StartY=-27.9037 StartZ=0 EndX=-47.8604 EndY=-27.9037 EndZ=0
    g9: LineSegment StartX=42.4722 StartY=-27.9037 StartZ=0 EndX=52.7411 EndY=-27.9037 EndZ=0
    g10: LineSegment StartX=59.2216 StartY=-12.599 StartZ=0 EndX=59.2216 EndY=-21.4232 EndZ=0
    g11: ArcOfCircle CenterX=52.7411 CenterY=-21.4232 CenterZ=0 NormalX=0 NormalY=0 NormalZ=1 AngleXU=0 Radius=6.4805 StartAngle=4.71239 EndAngle=6.28319
FEATURE [PartDesign::Pocket] Pocket005006
  BaseFeature = -> Pad003003007
  Length = 9
  Length2 = 100
  Profile = -> Sketch029
  Type = 0
FEATURE [PartDesign::Hole] Hole
  BaseFeature = -> Pocket005006
  Depth = 25
  DepthType = 1
  Diameter = 4.4
  DrillPoint = 1
  DrillPointAngle = 118
  HoleCutCountersinkAngle = 90
  HoleCutDepth = 0
  HoleCutDiameter = 4
  HoleCutType = 0
  ModelActualThread = false
  Profile = -> Sketch028
  Tapered = false
  TaperedAngle = 90
  ThreadAngle = 0
  ThreadClass = 0
  ThreadCutOffInner = 0
  ThreadCutOffOuter = 0
  ThreadDirection = 0
  ThreadFit = 0
  ThreadPitch = 0
  ThreadSize = 5
  ThreadType = 1
  Threaded = false
